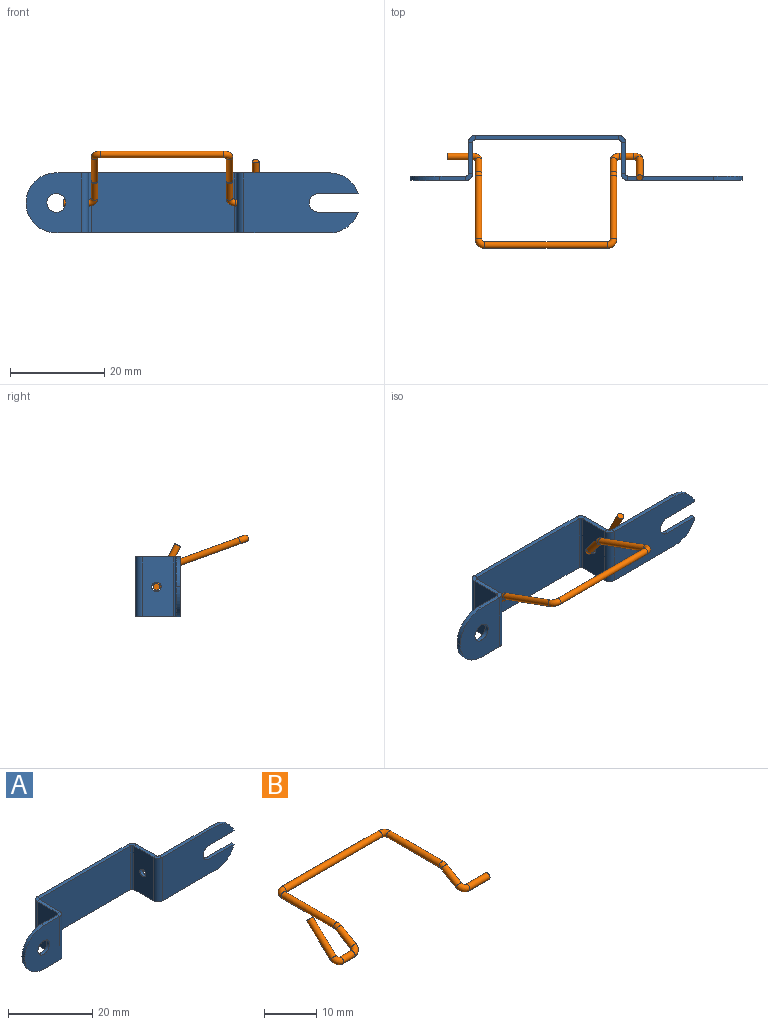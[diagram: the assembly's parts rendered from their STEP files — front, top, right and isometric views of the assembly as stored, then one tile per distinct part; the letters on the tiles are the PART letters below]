
ASSEMBLY  parts=2 mates=1
PART A: 46 faces, bbox 70.4x9.5x12.7 mm
  f0: plane 1.42x1.42mm, normal (0,0,1), area 1.4mm2, adj f1,f24,f27,f34
  f1: plane 6.68x0.91mm, normal (0,0,1), area 6.1mm2, adj f0,f4,f23,f28
  f2: plane 1.42x1.42mm, normal (0,0,-1), area 1.4mm2, adj f3,f7,f24,f27
  f3: plane 5.51x0.91mm, normal (0,0,-1), area 5mm2, adj f2,f25,f26,f39
  f4: plane 1.42x1.42mm, normal (0,0,1), area 1.4mm2, adj f1,f5,f22,f29
  f5: plane 30.49x0.91mm, normal (0,0,1), area 27.9mm2, adj f4,f8,f21,f30
  f6: plane 1.42x1.42mm, normal (0,0,-1), area 1.4mm2, adj f7,f11,f22,f29
  f7: plane 6.68x0.91mm, normal (0,0,-1), area 6.1mm2, adj f2,f6,f23,f28
  f8: plane 1.42x1.42mm, normal (0,0,1), area 1.4mm2, adj f5,f9,f20,f31
  f9: plane 6.68x0.91mm, normal (0,0,1), area 6.1mm2, adj f8,f12,f19,f32
  f10: plane 1.42x1.42mm, normal (0,0,-1), area 1.4mm2, adj f11,f15,f20,f31
  f11: plane 30.49x0.91mm, normal (0,0,-1), area 27.9mm2, adj f6,f10,f21,f30
  f12: plane 1.42x1.42mm, normal (0,0,1), area 1.4mm2, adj f9,f13,f18,f33
  f13: plane 18.16x0.91mm, normal (0,0,1), area 16.6mm2, adj f12,f16,f17,f36
  f14: plane 1.42x1.42mm, normal (0,0,-1), area 1.4mm2, adj f15,f18,f33,f35
  f15: plane 6.68x0.91mm, normal (0,0,-1), area 6.1mm2, adj f10,f14,f19,f32
  f16: plane 24.19x12.7mm, normal (0,-1,0), area 253.9mm2, adj f13,f33,f35,f36,f37,f41,f42,f43
  f17: plane 24.19x12.7mm, normal (0,1,0), area 253.9mm2, adj f13,f18,f35,f36,f37,f41,f42,f43
  f18: cylinder r=0.51mm len=12.7mm, axis (0,0,-1), area 10.1mm2, adj f12,f14,f17,f19
  f19: plane 12.7x6.68mm, normal (1,0,0), area 81.8mm2, adj f9,f15,f18,f20,f44
  f20: cylinder r=1.42mm len=12.7mm, axis (0,0,-1), area 28.4mm2, adj f8,f10,f19,f21
  f21: plane 30.49x12.7mm, normal (0,1,0), area 387.3mm2, adj f5,f11,f20,f22
  f22: cylinder r=1.42mm len=12.7mm, axis (0,0,-1), area 28.4mm2, adj f4,f6,f21,f23
  f23: plane 12.7x6.68mm, normal (-1,0,0), area 81.8mm2, adj f1,f7,f22,f24,f45
  f24: cylinder r=0.51mm len=12.7mm, axis (0,0,-1), area 10.1mm2, adj f0,f2,f23,f25
  f25: plane 12.7x11.86mm, normal (0,1,0), area 121mm2, adj f3,f24,f34,f38,f39,f40
  f26: plane 12.7x11.86mm, normal (0,-1,0), area 121mm2, adj f3,f27,f34,f38,f39,f40
  f27: cylinder r=1.42mm len=12.7mm, axis (0,0,-1), area 28.4mm2, adj f0,f2,f26,f28
  f28: plane 12.7x6.68mm, normal (1,0,0), area 81.8mm2, adj f1,f7,f27,f29,f45
  f29: cylinder r=0.51mm len=12.7mm, axis (0,0,-1), area 10.1mm2, adj f4,f6,f28,f30
  f30: plane 30.49x12.7mm, normal (0,-1,0), area 387.3mm2, adj f5,f11,f29,f31
  f31: cylinder r=0.51mm len=12.7mm, axis (0,0,-1), area 10.1mm2, adj f8,f10,f30,f32
  f32: plane 12.7x6.68mm, normal (-1,0,0), area 81.8mm2, adj f9,f15,f31,f33,f44
  f33: cylinder r=1.42mm len=12.7mm, axis (0,0,-1), area 28.4mm2, adj f12,f14,f16,f32
  f34: plane 5.51x0.91mm, normal (0,0,1), area 5mm2, adj f0,f25,f26,f38
  f35: plane 18.16x0.91mm, normal (0,0,-1), area 16.6mm2, adj f14,f16,f17,f37
  f36: cylinder r=6.35mm len=6.03mm, axis (0,-1,0), area 7.3mm2, adj f13,f16,f17,f43
  f37: cylinder r=6.35mm len=6.03mm, axis (0,-1,0), area 7.3mm2, adj f16,f17,f35,f42
  f38: cylinder r=6.35mm len=6.35mm, axis (0,-1,0), area 9.1mm2, adj f25,f26,f34,f39
  f39: cylinder r=6.35mm len=6.35mm, axis (0,1,0), area 9.1mm2, adj f3,f25,f26,f38
  f40: cylinder r=1.98mm len=3.96mm, axis (0,1,0), area 11.4mm2, adj f25,f26
  f41: cylinder r=1.98mm len=3.96mm, axis (0,1,0), area 5.7mm2, adj f16,f17,f42,f43
  f42: plane 8.34x0.91mm, normal (0,0,1), area 7.6mm2, adj f16,f17,f37,f41
  f43: plane 8.34x0.91mm, normal (0,0,-1), area 7.6mm2, adj f16,f17,f36,f41
  f44: cylinder r=0.99mm len=1.98mm, axis (-1,0,0), area 5.7mm2, adj f19,f32
  f45: cylinder r=0.99mm len=1.98mm, axis (-1,0,0), area 5.7mm2, adj f23,f28
PART B: 17 faces, bbox 41.7x22.9x8.1 mm
  f0: cylinder r=0.7mm len=7.28mm, axis (0,0.73,0.68), area 38mm2, adj f1,f15
  f1: torus R=1.27mm, axis (0,0.68,-0.73), area 8.8mm2, adj f0,f2
  f2: cylinder r=0.7mm len=3.05mm, axis (-1,0,0), area 13.4mm2, adj f1,f3
  f3: torus R=1.27mm, axis (0,0.52,-0.86), area 8.8mm2, adj f2,f4
  f4: cylinder r=0.7mm len=4.65mm, axis (0,-0.86,-0.52), area 20.1mm2, adj f3,f5
  f5: torus R=1.27mm, axis (1,0,0), area 3mm2, adj f4,f6
  f6: cylinder r=0.7mm len=14.25mm, axis (0,-1,0), area 62.6mm2, adj f5,f7
  f7: torus R=1.27mm, axis (0,0,1), area 8.8mm2, adj f6,f8
  f8: cylinder r=0.7mm len=26.04mm, axis (-1,0,0), area 114.3mm2, adj f7,f9
  f9: torus R=1.27mm, axis (0,0,1), area 8.8mm2, adj f8,f10
  f10: cylinder r=0.7mm len=14.25mm, axis (0,1,0), area 62.6mm2, adj f9,f11
  f11: torus R=1.27mm, axis (-1,0,0), area 3mm2, adj f10,f12
  f12: cylinder r=0.7mm len=4.65mm, axis (0,0.86,0.52), area 20.1mm2, adj f11,f13
  f13: torus R=1.27mm, axis (0,0.52,-0.86), area 8.8mm2, adj f12,f14
  f14: cylinder r=0.7mm len=5.42mm, axis (1,0,0), area 23.8mm2, adj f13,f16
  f15: plane 1.4x1.02mm, normal (0,0.73,0.68), area 1.5mm2, adj f0
  f16: plane 1.4x1.4mm, normal (1,0,0), area 1.5mm2, adj f14
PLACE A t=(-9.51,-2.17,-9.43)mm fixed
PLACE B rot(axis=(0,0.17,0.98),180deg) t=(-1.38,-16.83,0.83)mm
MATE revolute B.f14 <-> A.f44  axis (-1,0,0) through (-2.65,1.99,-9.43)mm
